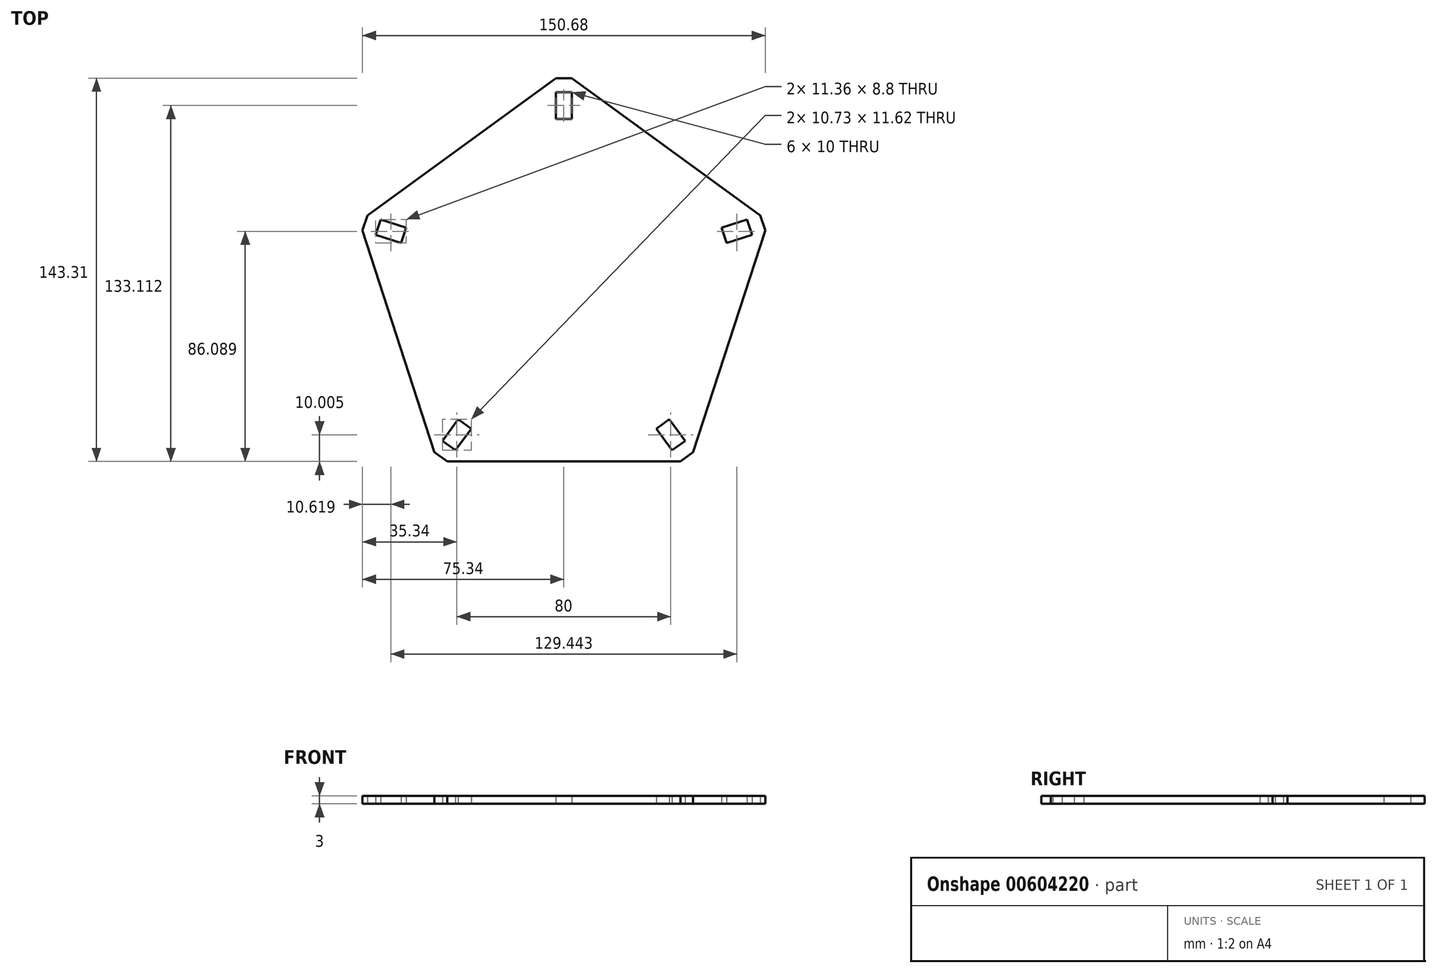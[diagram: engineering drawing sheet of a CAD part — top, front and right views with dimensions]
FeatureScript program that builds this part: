
annotation { "Feature Type Name" : "Feature", "Feature Type Description" : "" }
export const myFeature = defineFeature(function(context is Context, id is Id, definition is map)
    precondition{}
    {
        {
            var Q0;
            Q0=qCreatedBy(makeId("Top.planeOp"),FACE);
            var sketch = newSketch(context, id + "F0", { "sketchPlane" : qUnion([Q0])});
            skCircle(sketch, "E0.cCircle", {"center": v(0, 0) * mm, "radius": 68.05 * mm, "construction": true});
            skLineSegment(sketch, "E0.0", {"start": v(40, -55.06) * mm, "end": v(-40, -55.06) * mm, "construction": true});
            skLineSegment(sketch, "E0.1", {"start": v(-40, -55.06) * mm, "end": v(-64.72, 21.03) * mm, "construction": true});
            skLineSegment(sketch, "E0.2", {"start": v(-64.72, 21.03) * mm, "end": v(0, 68.05) * mm, "construction": true});
            skLineSegment(sketch, "E0.3", {"start": v(0, 68.05) * mm, "end": v(64.72, 21.03) * mm, "construction": true});
            skLineSegment(sketch, "E0.4", {"start": v(64.72, 21.03) * mm, "end": v(40, -55.06) * mm, "construction": true});
            skLineSegment(sketch, "E1.0", {"start": v(75.34, 21.35) * mm, "end": v(48.4, -61.56) * mm});
            skLineSegment(sketch, "E1.1", {"start": v(2.97, 78.25) * mm, "end": v(73.5, 27) * mm});
            skLineSegment(sketch, "E1.2", {"start": v(47.27, -65.06) * mm, "end": v(-47.27, -65.06) * mm, "construction": true});
            skLineSegment(sketch, "E1.3", {"start": v(-48.4, -61.56) * mm, "end": v(-75.34, 21.35) * mm});
            skLineSegment(sketch, "E1.4", {"start": v(-73.5, 27) * mm, "end": v(-2.97, 78.25) * mm});
            skLineSegment(sketch, "E2.bottom", {"start": v(3, 63.05) * mm, "end": v(-3, 63.05) * mm});
            skLineSegment(sketch, "E2.top", {"start": v(3, 73.05) * mm, "end": v(-3, 73.05) * mm});
            skLineSegment(sketch, "E2.left", {"start": v(3, 63.05) * mm, "end": v(3, 73.05) * mm});
            skLineSegment(sketch, "E2.right", {"start": v(-3, 63.05) * mm, "end": v(-3, 73.05) * mm});
            skPoint(sketch, "E2.middle", {"position": v(0, 68.05) * mm});
            skLineSegment(sketch, "E3", {"start": v(-2.97, 78.25) * mm, "end": v(2.97, 78.25) * mm});
            skLineSegment(sketch, "E4.1.0", {"start": v(-59.04, 22.34) * mm, "end": v(-68.55, 25.43) * mm});
            skLineSegment(sketch, "E4.1.1", {"start": v(-68.55, 25.43) * mm, "end": v(-70.4, 19.72) * mm});
            skLineSegment(sketch, "E4.1.2", {"start": v(-60.9, 16.63) * mm, "end": v(-70.4, 19.72) * mm});
            skLineSegment(sketch, "E4.1.3", {"start": v(-59.04, 22.34) * mm, "end": v(-60.9, 16.63) * mm});
            skLineSegment(sketch, "E4.1.4", {"start": v(-75.34, 21.35) * mm, "end": v(-73.5, 27) * mm});
            skLineSegment(sketch, "E4.2.0", {"start": v(-39.49, -49.25) * mm, "end": v(-45.37, -57.34) * mm});
            skLineSegment(sketch, "E4.2.1", {"start": v(-45.37, -57.34) * mm, "end": v(-40.51, -60.86) * mm});
            skLineSegment(sketch, "E4.2.2", {"start": v(-34.63, -52.77) * mm, "end": v(-40.51, -60.86) * mm});
            skLineSegment(sketch, "E4.2.3", {"start": v(-39.49, -49.25) * mm, "end": v(-34.63, -52.77) * mm});
            skLineSegment(sketch, "E4.2.4", {"start": v(-43.59, -65.06) * mm, "end": v(-48.4, -61.56) * mm});
            skLineSegment(sketch, "E4.3.0", {"start": v(34.63, -52.77) * mm, "end": v(40.51, -60.86) * mm});
            skLineSegment(sketch, "E4.3.1", {"start": v(40.51, -60.86) * mm, "end": v(45.37, -57.34) * mm});
            skLineSegment(sketch, "E4.3.2", {"start": v(39.49, -49.25) * mm, "end": v(45.37, -57.34) * mm});
            skLineSegment(sketch, "E4.3.3", {"start": v(34.63, -52.77) * mm, "end": v(39.49, -49.25) * mm});
            skLineSegment(sketch, "E4.3.4", {"start": v(48.4, -61.56) * mm, "end": v(43.59, -65.06) * mm});
            skLineSegment(sketch, "E4.4.0", {"start": v(60.9, 16.63) * mm, "end": v(70.4, 19.72) * mm});
            skLineSegment(sketch, "E4.4.1", {"start": v(70.4, 19.72) * mm, "end": v(68.55, 25.43) * mm});
            skLineSegment(sketch, "E4.4.2", {"start": v(59.04, 22.34) * mm, "end": v(68.55, 25.43) * mm});
            skLineSegment(sketch, "E4.4.3", {"start": v(60.9, 16.63) * mm, "end": v(59.04, 22.34) * mm});
            skLineSegment(sketch, "E4.4.4", {"start": v(73.5, 27) * mm, "end": v(75.34, 21.35) * mm});
            skLineSegment(sketch, "E5", {"start": v(-43.59, -65.06) * mm, "end": v(43.59, -65.06) * mm});
            skSolve(sketch);
        }
        {
            var Q0;
            Q0 = qSketchRegion(id + "F0", true);
            extrude(context, id + "F1", {"entities" : qUnion([Q0]), "depth" : 3 * mm, "offsetDistance" : 25 * mm});
        }
    });
